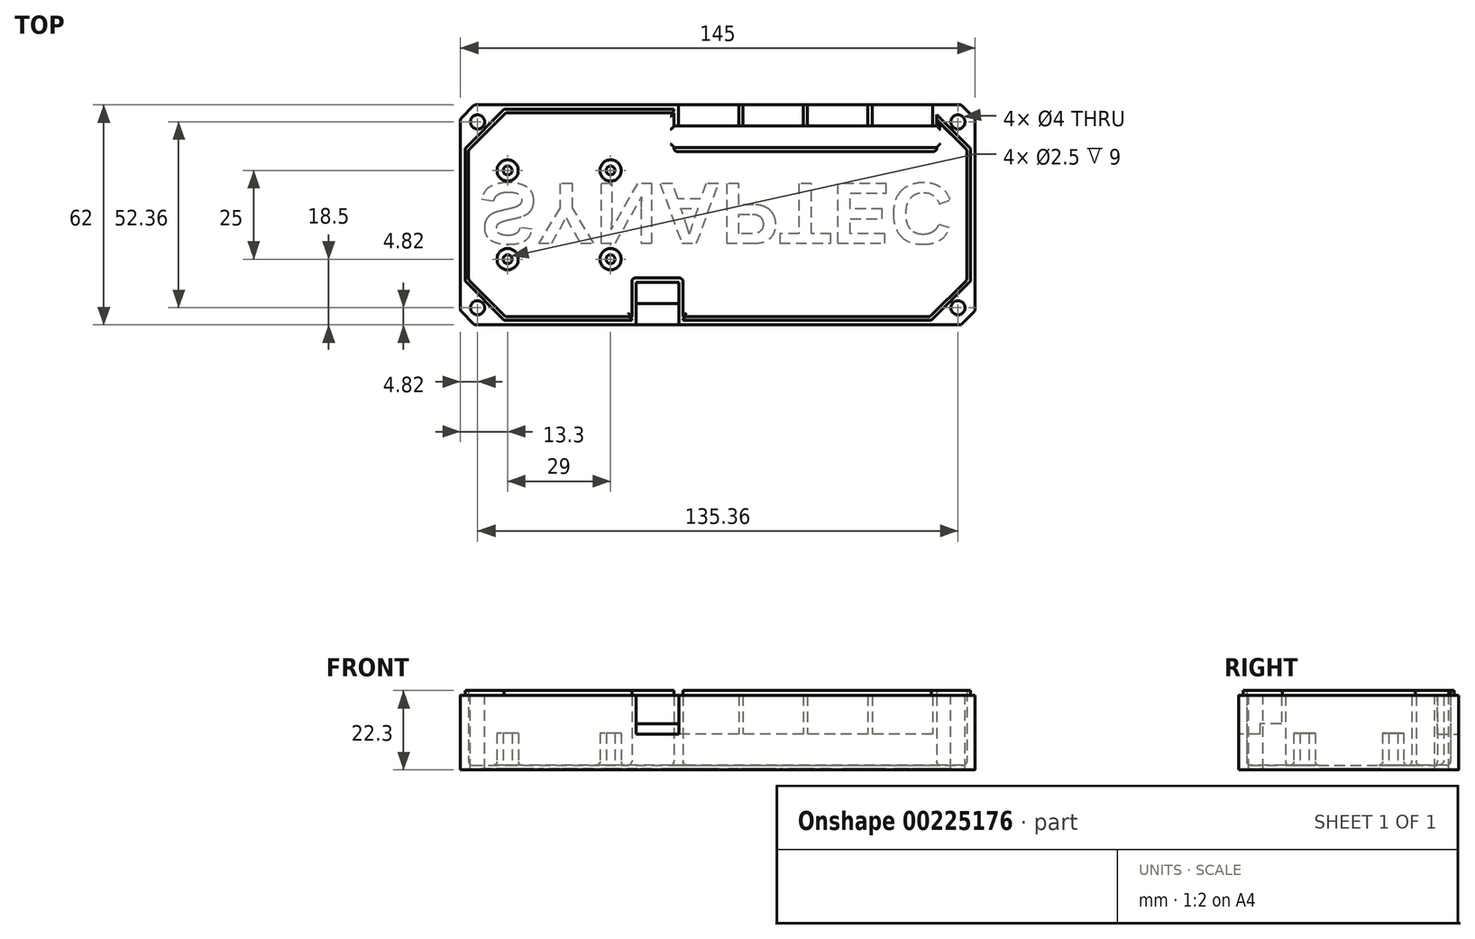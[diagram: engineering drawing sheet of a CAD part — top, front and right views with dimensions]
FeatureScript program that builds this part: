
annotation { "Feature Type Name" : "Feature", "Feature Type Description" : "" }
export const myFeature = defineFeature(function(context is Context, id is Id, definition is map)
    precondition{}
    {
        {
            var Q0;
            Q0=qCreatedBy(makeId("Top.planeOp"),FACE);
            var sketch = newSketch(context, id + "F0", { "sketchPlane" : qUnion([Q0])});
            skLineSegment(sketch, "E0.bottom", {"start": v(72.5, -31) * mm, "end": v(-72.5, -31) * mm});
            skLineSegment(sketch, "E0.top", {"start": v(72.5, 31) * mm, "end": v(-72.5, 31) * mm});
            skLineSegment(sketch, "E0.left", {"start": v(72.5, -31) * mm, "end": v(72.5, 31) * mm});
            skLineSegment(sketch, "E0.right", {"start": v(-72.5, -31) * mm, "end": v(-72.5, 31) * mm});
            skPoint(sketch, "E0.middle", {"position": v(0, 0) * mm});
            skSolve(sketch);
        }
        {
            var Q0;
            Q0=qSketchRegion(id+"F0",true);
            extrude(context, id + "F1", {"entities" : qUnion([Q0]), "depth" : 21 * mm});
        }
        {
            var Q0;
            Q0=makeQuery(id+"F1.opExtrude","CAP_FACE",FACE,{"disambiguationData":[OSD([sQuery(id+"F0.wireOp",EDGE,"E0.bottom"),sQuery(id+"F0.wireOp",EDGE,"E0.top"),sQuery(id+"F0.wireOp",EDGE,"E0.left"),sQuery(id+"F0.wireOp",EDGE,"E0.right")])],"isStart":false});
            var Q1;
            Q1=makeQuery(id+"F1.opExtrude","SWEPT_BODY",BODY,{"disambiguationData":[OSD([sQuery(id+"F0.wireOp",EDGE,"E0.bottom"),sQuery(id+"F0.wireOp",EDGE,"E0.top"),sQuery(id+"F0.wireOp",EDGE,"E0.left"),sQuery(id+"F0.wireOp",EDGE,"E0.right")])]});
            shell(context, id + "F2", {"entities" : qUnion([Q0]), "parts" : qUnion([Q1]), "thickness" : 1.3 * mm});
        }
        {
            var Q0;
            Q0=makeQuery(id+"F2.opShell","OFFSET_EDGE",EDGE,{"disambiguationData":[OSD([sQuery(id+"F0.wireOp",EDGE,"E0.top"),sQuery(id+"F0.wireOp",EDGE,"E0.left")])]});
            var Q1;
            Q1=makeQuery(id+"F2.opShell","OFFSET_EDGE",EDGE,{"disambiguationData":[OSD([sQuery(id+"F0.wireOp",EDGE,"E0.top"),sQuery(id+"F0.wireOp",EDGE,"E0.right")])]});
            var Q2;
            Q2=makeQuery(id+"F2.opShell","OFFSET_EDGE",EDGE,{"disambiguationData":[OSD([sQuery(id+"F0.wireOp",EDGE,"E0.bottom"),sQuery(id+"F0.wireOp",EDGE,"E0.right")])]});
            var Q3;
            Q3=makeQuery(id+"F2.opShell","OFFSET_EDGE",EDGE,{"disambiguationData":[OSD([sQuery(id+"F0.wireOp",EDGE,"E0.bottom"),sQuery(id+"F0.wireOp",EDGE,"E0.left")])]});
            chamfer(context, id + "F3", {"entities" : qUnion([Q0, Q1, Q2, Q3]), "width" : 11 * mm, "tangentPropagation" : true});
        }
        {
            var Q0;
            Q0=makeQuery(id+"F1.opExtrude","SWEPT_EDGE",EDGE,{"disambiguationData":[OSD([sQuery(id+"F0.wireOp",EDGE,"E0.top"),sQuery(id+"F0.wireOp",EDGE,"E0.right")])]});
            var Q1;
            Q1=makeQuery(id+"F1.opExtrude","SWEPT_EDGE",EDGE,{"disambiguationData":[OSD([sQuery(id+"F0.wireOp",EDGE,"E0.bottom"),sQuery(id+"F0.wireOp",EDGE,"E0.right")])]});
            var Q2;
            Q2=makeQuery(id+"F1.opExtrude","SWEPT_EDGE",EDGE,{"disambiguationData":[OSD([sQuery(id+"F0.wireOp",EDGE,"E0.top"),sQuery(id+"F0.wireOp",EDGE,"E0.left")])]});
            var Q3;
            Q3=makeQuery(id+"F1.opExtrude","SWEPT_EDGE",EDGE,{"disambiguationData":[OSD([sQuery(id+"F0.wireOp",EDGE,"E0.bottom"),sQuery(id+"F0.wireOp",EDGE,"E0.left")])]});
            chamfer(context, id + "F4", {"entities" : qUnion([Q0, Q1, Q2, Q3]), "width" : 4 * mm, "tangentPropagation" : true});
        }
        {
            var Q0;
            Q0=makeQuery(id+"F1.opExtrude","CAP_FACE",FACE,{"disambiguationData":[OSD([sQuery(id+"F0.wireOp",EDGE,"E0.bottom"),sQuery(id+"F0.wireOp",EDGE,"E0.top"),sQuery(id+"F0.wireOp",EDGE,"E0.left"),sQuery(id+"F0.wireOp",EDGE,"E0.right")])],"isStart":false});
            var sketch = newSketch(context, id + "F5", { "sketchPlane" : qUnion([Q0])});
            skCircle(sketch, "E1", {"center": v(-67.68, -26.18) * mm, "radius": 2 * mm});
            skCircle(sketch, "E2", {"center": v(-67.68, 26.18) * mm, "radius": 2 * mm});
            skCircle(sketch, "E3", {"center": v(67.68, 26.18) * mm, "radius": 2 * mm});
            skCircle(sketch, "E4", {"center": v(67.68, -26.18) * mm, "radius": 2 * mm});
            skLineSegment(sketch, "E5", {"start": v(-70.5, -29) * mm, "end": v(-65.7, -24.2) * mm, "construction": true});
            skLineSegment(sketch, "E6", {"start": v(-70.5, 29) * mm, "end": v(-65.7, 24.2) * mm, "construction": true});
            skLineSegment(sketch, "E7", {"start": v(70.5, 29) * mm, "end": v(65.7, 24.2) * mm, "construction": true});
            skLineSegment(sketch, "E8", {"start": v(70.5, -29) * mm, "end": v(65.7, -24.2) * mm, "construction": true});
            skSolve(sketch);
        }
        {
            var Q0;
            Q0=makeQuery(id+"F5.imprint","IMPRINT",FACE,{"disambiguationData":[TD([[makeQuery(id+"F5.imprint","IMPRINT",EDGE,{"derivedFrom":sQuery(id+"F5.wireOp",EDGE,"E2")}),1.0]])]});
            var Q1;
            Q1=makeQuery(id+"F5.imprint","IMPRINT",FACE,{"disambiguationData":[TD([[makeQuery(id+"F5.imprint","IMPRINT",EDGE,{"derivedFrom":sQuery(id+"F5.wireOp",EDGE,"E1")}),1.0]])]});
            var Q2;
            Q2=makeQuery(id+"F5.imprint","IMPRINT",FACE,{"disambiguationData":[TD([[makeQuery(id+"F5.imprint","IMPRINT",EDGE,{"derivedFrom":sQuery(id+"F5.wireOp",EDGE,"E4")}),1.0]])]});
            var Q3;
            Q3=makeQuery(id+"F5.imprint","IMPRINT",FACE,{"disambiguationData":[TD([[makeQuery(id+"F5.imprint","IMPRINT",EDGE,{"derivedFrom":sQuery(id+"F5.wireOp",EDGE,"E3")}),1.0]])]});
            extrude(context, id + "F6", {"entities" : qUnion([Q0, Q1, Q2, Q3]), "operationType" : NewBodyOperationType.REMOVE, "endBound" : BoundingType.UP_TO_NEXT, "oppositeDirection" : true, "depth" : 15 * mm});
        }
        {
            var Q0;
            Q0=makeQuery(id+"F2.opShell","OFFSET_FACE",FACE,{"disambiguationData":[OSD([sQuery(id+"F0.wireOp",EDGE,"E0.bottom"),sQuery(id+"F0.wireOp",EDGE,"E0.top"),sQuery(id+"F0.wireOp",EDGE,"E0.left"),sQuery(id+"F0.wireOp",EDGE,"E0.right")])]});
            var sketch = newSketch(context, id + "F7", { "sketchPlane" : qUnion([Q0])});
            skCircle(sketch, "E9", {"center": v(-30.2, -12.5) * mm, "radius": 3 * mm});
            skCircle(sketch, "E10.0", {"center": v(-30.2, -12.5) * mm, "radius": 1.25 * mm});
            skCircle(sketch, "E11.0.1.0", {"center": v(-30.2, 12.5) * mm, "radius": 3 * mm});
            skCircle(sketch, "E11.0.1.1", {"center": v(-30.2, 12.5) * mm, "radius": 1.25 * mm});
            skCircle(sketch, "E11.1.0.0", {"center": v(-59.2, -12.5) * mm, "radius": 3 * mm});
            skCircle(sketch, "E11.1.0.1", {"center": v(-59.2, -12.5) * mm, "radius": 1.25 * mm});
            skCircle(sketch, "E11.1.1.0", {"center": v(-59.2, 12.5) * mm, "radius": 3 * mm});
            skCircle(sketch, "E11.1.1.1", {"center": v(-59.2, 12.5) * mm, "radius": 1.25 * mm});
            skLineSegment(sketch, "E11.direction1", {"start": v(-30.2, -12.5) * mm, "end": v(-59.2, -12.5) * mm, "construction": true});
            skLineSegment(sketch, "E11.direction2", {"start": v(-30.2, -12.5) * mm, "end": v(-30.2, 12.5) * mm, "construction": true});
            skLineSegment(sketch, "E12.right", {"start": v(71.2, 18) * mm, "end": v(71.2, 16.8) * mm});
            skLineSegment(sketch, "E13.bottom", {"start": v(61.7, 29.7) * mm, "end": v(-12.3, 29.7) * mm});
            skLineSegment(sketch, "E13.top", {"start": v(61.7, 25) * mm, "end": v(-12.3, 25) * mm});
            skLineSegment(sketch, "E13.left", {"start": v(61.7, 29.7) * mm, "end": v(61.7, 25) * mm});
            skLineSegment(sketch, "E13.right", {"start": v(-12.3, 29.7) * mm, "end": v(-12.3, 25) * mm});
            skLineSegment(sketch, "E14.bottom", {"start": v(-12.3, 25) * mm, "end": v(61.7, 25) * mm});
            skLineSegment(sketch, "E14.top", {"start": v(-12.3, 19) * mm, "end": v(61.7, 19) * mm});
            skLineSegment(sketch, "E14.left", {"start": v(-12.3, 25) * mm, "end": v(-12.3, 19) * mm});
            skLineSegment(sketch, "E14.right", {"start": v(61.7, 25) * mm, "end": v(61.7, 19) * mm});
            skLineSegment(sketch, "E15.top", {"start": v(-12.3, 17.8) * mm, "end": v(61.7, 17.8) * mm});
            skLineSegment(sketch, "E15.left", {"start": v(-12.3, 19) * mm, "end": v(-12.3, 17.8) * mm});
            skLineSegment(sketch, "E15.right", {"start": v(61.7, 19) * mm, "end": v(61.7, 17.8) * mm});
            skLineSegment(sketch, "E16.bottom", {"start": v(-24.2, -29.7) * mm, "end": v(-9.8, -29.7) * mm});
            skLineSegment(sketch, "E16.top", {"start": v(-24.2, -25) * mm, "end": v(-9.8, -25) * mm});
            skLineSegment(sketch, "E16.left", {"start": v(-24.2, -29.7) * mm, "end": v(-24.2, -25) * mm});
            skLineSegment(sketch, "E16.right", {"start": v(-9.8, -29.7) * mm, "end": v(-9.8, -25) * mm});
            skLineSegment(sketch, "E17.top", {"start": v(-24.2, -19) * mm, "end": v(-9.8, -19) * mm});
            skLineSegment(sketch, "E17.left", {"start": v(-24.2, -25) * mm, "end": v(-24.2, -19) * mm});
            skLineSegment(sketch, "E17.right", {"start": v(-9.8, -25) * mm, "end": v(-9.8, -19) * mm});
            skLineSegment(sketch, "E18.top", {"start": v(-24.2, -17.8) * mm, "end": v(-9.8, -17.8) * mm});
            skLineSegment(sketch, "E18.left", {"start": v(-24.2, -19) * mm, "end": v(-24.2, -17.8) * mm});
            skLineSegment(sketch, "E18.right", {"start": v(-9.8, -19) * mm, "end": v(-9.8, -17.8) * mm});
            skSolve(sketch);
        }
        {
            var Q0;
            Q0=makeQuery(id+"F7.imprint","IMPRINT",FACE,{"disambiguationData":[TD([[makeQuery(id+"F7.imprint","IMPRINT",EDGE,{"derivedFrom":sQuery(id+"F7.wireOp",EDGE,"E9")}),1.0]])]});
            var Q1;
            Q1=makeQuery(id+"F7.imprint","IMPRINT",FACE,{"disambiguationData":[TD([[makeQuery(id+"F7.imprint","IMPRINT",EDGE,{"derivedFrom":sQuery(id+"F7.wireOp",EDGE,"E11.0.1.0")}),1.0]])]});
            var Q2;
            Q2=makeQuery(id+"F7.imprint","IMPRINT",FACE,{"disambiguationData":[TD([[makeQuery(id+"F7.imprint","IMPRINT",EDGE,{"derivedFrom":sQuery(id+"F7.wireOp",EDGE,"E11.1.1.0")}),1.0]])]});
            var Q3;
            Q3=makeQuery(id+"F7.imprint","IMPRINT",FACE,{"disambiguationData":[TD([[makeQuery(id+"F7.imprint","IMPRINT",EDGE,{"derivedFrom":sQuery(id+"F7.wireOp",EDGE,"E11.1.0.0")}),1.0]])]});
            var Q4;
            Q4=makeQuery(id+"F7.imprint","IMPRINT",FACE,{"disambiguationData":[TD([[makeQuery(id+"F7.imprint","IMPRINT",EDGE,{"derivedFrom":sQuery(id+"F7.wireOp",EDGE,"42ae70fa-aec6-44d3-95c4-a3b67ad8d79e.1.1.0")}),1.0]])]});
            var Q5;
            Q5=makeQuery(id+"F7.imprint","IMPRINT",FACE,{"disambiguationData":[TD([[makeQuery(id+"F7.imprint","IMPRINT",EDGE,{"derivedFrom":sQuery(id+"F7.wireOp",EDGE,"42ae70fa-aec6-44d3-95c4-a3b67ad8d79e.0.1.0")}),1.0]])]});
            var Q6;
            Q6=makeQuery(id+"F7.imprint","IMPRINT",FACE,{"disambiguationData":[TD([[makeQuery(id+"F7.imprint","IMPRINT",EDGE,{"derivedFrom":sQuery(id+"F7.wireOp",EDGE,"ABs4xrQX-9s09-FMAu-MQul-4i9KuJrflMF1.bottom")}),-1.0]])]});
            var Q7;
            Q7=makeQuery(id+"F7.imprint","IMPRINT",FACE,{"disambiguationData":[TD([[makeQuery(id+"F7.imprint","IMPRINT",EDGE,{"derivedFrom":sQuery(id+"F7.wireOp",EDGE,"42ae70fa-aec6-44d3-95c4-a3b67ad8d79e.1.0.0")}),1.0]])]});
            extrude(context, id + "F8", {"entities" : qUnion([Q0, Q1, Q2, Q3, Q4, Q5, Q6, Q7]), "operationType" : NewBodyOperationType.ADD, "depth" : 9 * mm});
        }
        {
            var Q0;
            Q0=makeQuery(id+"F7.imprint","IMPRINT",FACE,{"disambiguationData":[TD([[makeQuery(id+"F7.imprint","IMPRINT",EDGE,{"derivedFrom":sQuery(id+"F7.wireOp",EDGE,"E13.bottom")}),1.0]])]});
            var Q1;
            Q1=makeQuery(id+"F7.imprint","IMPRINT",FACE,{"disambiguationData":[TD([[makeQuery(id+"F7.imprint","IMPRINT",EDGE,{"derivedFrom":sQuery(id+"F7.wireOp",EDGE,"E14.bottom")}),-1.0]])]});
            var Q2;
            Q2=makeQuery(id+"F7.imprint","IMPRINT",FACE,{"disambiguationData":[TD([[makeQuery(id+"F7.imprint","IMPRINT",EDGE,{"derivedFrom":sQuery(id+"F7.wireOp",EDGE,"E14.top")}),-1.0]])]});
            var Q3;
            Q3=makeQuery(id+"F7.imprint","IMPRINT",FACE,{"disambiguationData":[TD([[makeQuery(id+"F7.imprint","IMPRINT",EDGE,{"derivedFrom":sQuery(id+"F7.wireOp",EDGE,"E16.bottom")}),-1.0]])]});
            var Q4;
            Q4=makeQuery(id+"F7.imprint","IMPRINT",FACE,{"disambiguationData":[TD([[makeQuery(id+"F7.imprint","IMPRINT",EDGE,{"derivedFrom":sQuery(id+"F7.wireOp",EDGE,"E16.top")}),1.0]])]});
            var Q5;
            Q5=makeQuery(id+"F7.imprint","IMPRINT",FACE,{"disambiguationData":[TD([[makeQuery(id+"F7.imprint","IMPRINT",EDGE,{"derivedFrom":sQuery(id+"F7.wireOp",EDGE,"E17.top")}),1.0]])]});
            var Q6;
            {var subQ1=sQuery(id+"F7.wireOp",EDGE,"E13.right");Q6=makeQuery(id+"F7.imprint","IMPRINT",FACE,{"disambiguationData":[TD([[makeQuery(id+"F7.imprint","IMPRINT",EDGE,{"derivedFrom":subQ1}),1.0]])]});}
            var Q7;
            Q7=makeQuery(id+"F1.opExtrude","CAP_FACE",FACE,{"disambiguationData":[OSD([sQuery(id+"F0.wireOp",EDGE,"E0.bottom"),sQuery(id+"F0.wireOp",EDGE,"E0.top"),sQuery(id+"F0.wireOp",EDGE,"E0.left"),sQuery(id+"F0.wireOp",EDGE,"E0.right")])],"isStart":false});
            extrude(context, id + "F9", {"entities" : qUnion([Q0, Q1, Q2, Q3, Q4, Q5, Q6]), "operationType" : NewBodyOperationType.ADD, "endBound" : BoundingType.UP_TO_SURFACE, "endBoundEntityFace" : qUnion([Q7]), "depth" : 15 * mm});
        }
        {
            var Q0;
            {var subQ0=sQuery(id+"F0.wireOp",EDGE,"E0.right");var subQ1=sQuery(id+"F0.wireOp",EDGE,"E0.top");var subQ2=sQuery(id+"F0.wireOp",EDGE,"E0.left");var subQ3=sQuery(id+"F0.wireOp",EDGE,"E0.bottom");Q0=makeQuery(id+"F8.boolean.opBoolean","SPLIT",FACE,{"disambiguationData":[TD([makeQuery(id+"F2.opShell","OFFSET_FACE",FACE,{"disambiguationData":[OSD([subQ3])]})])],"derivedFrom":makeQuery(id+"F2.opShell","OFFSET_FACE",FACE,{"disambiguationData":[OSD([subQ3,subQ1,subQ2,subQ0])]})});}
            var sketch = newSketch(context, id + "F10", { "sketchPlane" : qUnion([Q0])});
            skLineSegment(sketch, "E19.2", {"start": v(-59.79, -28.7) * mm, "end": v(-24.2, -28.7) * mm});
            skLineSegment(sketch, "E19.3", {"start": v(-70.2, -18.29) * mm, "end": v(-59.79, -28.7) * mm});
            skLineSegment(sketch, "E19.4", {"start": v(70.2, 18.29) * mm, "end": v(61.7, 26.79) * mm});
            skLineSegment(sketch, "E19.5", {"start": v(70.2, -18.29) * mm, "end": v(70.2, 18.29) * mm});
            skLineSegment(sketch, "E19.6", {"start": v(59.79, -28.7) * mm, "end": v(70.2, -18.29) * mm});
            skLineSegment(sketch, "E19.7", {"start": v(-9.8, -28.7) * mm, "end": v(59.79, -28.7) * mm});
            skLineSegment(sketch, "E19.11", {"start": v(-12.3, 28.7) * mm, "end": v(-59.79, 28.7) * mm});
            skLineSegment(sketch, "E19.13", {"start": v(-59.79, 28.7) * mm, "end": v(-70.2, 18.29) * mm});
            skLineSegment(sketch, "E19.14", {"start": v(-70.2, 18.29) * mm, "end": v(-70.2, -18.29) * mm});
            skSolve(sketch);
        }
        {
            var Q0;
            Q0=makeQuery(id+"F10.imprint","IMPRINT",FACE,{"disambiguationData":[TD([[makeQuery(id+"F10.imprint","IMPRINT",EDGE,{"derivedFrom":sQuery(id+"F10.wireOp",EDGE,"E19.0")}),-1.0]])]});
            var Q1;
            {var subQ9=sQuery(id+"F10.wireOp",EDGE,"E19.2");Q1=makeQuery(id+"F10.imprint","IMPRINT",FACE,{"disambiguationData":[TD([[makeQuery(id+"F10.imprint","IMPRINT",EDGE,{"derivedFrom":subQ9}),-1.0]])]});}
            var Q2;
            {var subQ9=sQuery(id+"F10.wireOp",EDGE,"E19.4");Q2=makeQuery(id+"F10.imprint","IMPRINT",FACE,{"disambiguationData":[TD([[makeQuery(id+"F10.imprint","IMPRINT",EDGE,{"derivedFrom":subQ9}),-1.0]])]});}
            extrude(context, id + "F11", {"entities" : qUnion([Q0, Q1, Q2]), "operationType" : NewBodyOperationType.ADD, "depth" : 21 * mm});
        }
        {
            var Q0;
            Q0=makeQuery(id+"F1.opExtrude","SWEPT_FACE",FACE,{"disambiguationData":[OSD([sQuery(id+"F0.wireOp",EDGE,"E0.top")])]});
            var sketch = newSketch(context, id + "F12", { "sketchPlane" : qUnion([Q0])});
            skLineSegment(sketch, "E20.bottom", {"start": v(-60.5, 21) * mm, "end": v(-43.5, 21) * mm});
            skLineSegment(sketch, "E20.top", {"start": v(-60.5, 10) * mm, "end": v(-43.5, 10) * mm});
            skLineSegment(sketch, "E20.left", {"start": v(-60.5, 21) * mm, "end": v(-60.5, 10) * mm});
            skLineSegment(sketch, "E20.right", {"start": v(-43.5, 21) * mm, "end": v(-43.5, 10) * mm});
            skLineSegment(sketch, "E21", {"start": v(-60.5, 13) * mm, "end": v(-43.5, 13) * mm});
            skLineSegment(sketch, "E22.1.0.0", {"start": v(-42.3, 21) * mm, "end": v(-42.3, 10) * mm});
            skLineSegment(sketch, "E22.1.0.1", {"start": v(-25.3, 21) * mm, "end": v(-25.3, 10) * mm});
            skLineSegment(sketch, "E22.1.0.2", {"start": v(-42.3, 13) * mm, "end": v(-25.3, 13) * mm});
            skLineSegment(sketch, "E22.1.0.3", {"start": v(-42.3, 10) * mm, "end": v(-25.3, 10) * mm});
            skLineSegment(sketch, "E22.1.0.4", {"start": v(-42.3, 21) * mm, "end": v(-25.3, 21) * mm});
            skLineSegment(sketch, "E22.2.0.0", {"start": v(-24.1, 21) * mm, "end": v(-24.1, 10) * mm});
            skLineSegment(sketch, "E22.2.0.1", {"start": v(-7.1, 21) * mm, "end": v(-7.1, 10) * mm});
            skLineSegment(sketch, "E22.2.0.2", {"start": v(-24.1, 13) * mm, "end": v(-7.1, 13) * mm});
            skLineSegment(sketch, "E22.2.0.3", {"start": v(-24.1, 10) * mm, "end": v(-7.1, 10) * mm});
            skLineSegment(sketch, "E22.2.0.4", {"start": v(-24.1, 21) * mm, "end": v(-7.1, 21) * mm});
            skLineSegment(sketch, "E22.3.0.0", {"start": v(-5.9, 21) * mm, "end": v(-5.9, 10) * mm});
            skLineSegment(sketch, "E22.3.0.1", {"start": v(11.1, 21) * mm, "end": v(11.1, 10) * mm});
            skLineSegment(sketch, "E22.3.0.2", {"start": v(-5.9, 13) * mm, "end": v(11.1, 13) * mm});
            skLineSegment(sketch, "E22.3.0.3", {"start": v(-5.9, 10) * mm, "end": v(11.1, 10) * mm});
            skLineSegment(sketch, "E22.3.0.4", {"start": v(-5.9, 21) * mm, "end": v(11.1, 21) * mm});
            skLineSegment(sketch, "E22.direction1", {"start": v(-60.5, 10) * mm, "end": v(-42.3, 10) * mm, "construction": true});
            skSolve(sketch);
        }
        {
            var Q0;
            {var subQ0=sQuery(id+"F12.wireOp",EDGE,"E21");Q0=makeQuery(id+"F12.imprint","IMPRINT",FACE,{"disambiguationData":[TD([[makeQuery(id+"F12.imprint","IMPRINT",EDGE,{"derivedFrom":subQ0}),1.0]])]});}
            var Q1;
            {var subQ0=sQuery(id+"F12.wireOp",EDGE,"E22.1.0.2");Q1=makeQuery(id+"F12.imprint","IMPRINT",FACE,{"disambiguationData":[TD([[makeQuery(id+"F12.imprint","IMPRINT",EDGE,{"derivedFrom":subQ0}),1.0]])]});}
            var Q2;
            {var subQ0=sQuery(id+"F12.wireOp",EDGE,"E22.2.0.2");Q2=makeQuery(id+"F12.imprint","IMPRINT",FACE,{"disambiguationData":[TD([[makeQuery(id+"F12.imprint","IMPRINT",EDGE,{"derivedFrom":subQ0}),1.0]])]});}
            var Q3;
            {var subQ0=sQuery(id+"F12.wireOp",EDGE,"E22.3.0.2");Q3=makeQuery(id+"F12.imprint","IMPRINT",FACE,{"disambiguationData":[TD([[makeQuery(id+"F12.imprint","IMPRINT",EDGE,{"derivedFrom":subQ0}),1.0]])]});}
            var Q4;
            {var subQ0=sQuery(id+"F12.wireOp",EDGE,"E22.3.0.4");Q4=makeQuery(id+"F12.imprint","IMPRINT",FACE,{"disambiguationData":[TD([[makeQuery(id+"F12.imprint","IMPRINT",EDGE,{"derivedFrom":subQ0}),-1.0]])]});}
            var Q5;
            {var subQ0=sQuery(id+"F12.wireOp",EDGE,"E22.2.0.4");Q5=makeQuery(id+"F12.imprint","IMPRINT",FACE,{"disambiguationData":[TD([[makeQuery(id+"F12.imprint","IMPRINT",EDGE,{"derivedFrom":subQ0}),-1.0]])]});}
            var Q6;
            {var subQ0=sQuery(id+"F12.wireOp",EDGE,"E22.1.0.4");Q6=makeQuery(id+"F12.imprint","IMPRINT",FACE,{"disambiguationData":[TD([[makeQuery(id+"F12.imprint","IMPRINT",EDGE,{"derivedFrom":subQ0}),-1.0]])]});}
            var Q7;
            {var subQ0=sQuery(id+"F12.wireOp",EDGE,"E20.bottom");Q7=makeQuery(id+"F12.imprint","IMPRINT",FACE,{"disambiguationData":[TD([[makeQuery(id+"F12.imprint","IMPRINT",EDGE,{"derivedFrom":subQ0}),-1.0]])]});}
            extrude(context, id + "F13", {"entities" : qUnion([Q0, Q1, Q2, Q3, Q4, Q5, Q6, Q7]), "operationType" : NewBodyOperationType.REMOVE, "oppositeDirection" : true, "depth" : 12 * mm});
        }
        {
            var Q0;
            {var subQ0=sQuery(id+"F12.wireOp",EDGE,"E20.top");Q0=makeQuery(id+"F12.imprint","IMPRINT",FACE,{"disambiguationData":[TD([[makeQuery(id+"F12.imprint","IMPRINT",EDGE,{"derivedFrom":subQ0}),1.0]])]});}
            var Q1;
            {var subQ2=sQuery(id+"F12.wireOp",EDGE,"E22.1.0.2");Q1=makeQuery(id+"F12.imprint","IMPRINT",FACE,{"disambiguationData":[TD([[makeQuery(id+"F12.imprint","IMPRINT",EDGE,{"derivedFrom":subQ2}),-1.0]])]});}
            var Q2;
            {var subQ2=sQuery(id+"F12.wireOp",EDGE,"E22.2.0.2");Q2=makeQuery(id+"F12.imprint","IMPRINT",FACE,{"disambiguationData":[TD([[makeQuery(id+"F12.imprint","IMPRINT",EDGE,{"derivedFrom":subQ2}),-1.0]])]});}
            var Q3;
            {var subQ2=sQuery(id+"F12.wireOp",EDGE,"E22.3.0.2");Q3=makeQuery(id+"F12.imprint","IMPRINT",FACE,{"disambiguationData":[TD([[makeQuery(id+"F12.imprint","IMPRINT",EDGE,{"derivedFrom":subQ2}),-1.0]])]});}
            extrude(context, id + "F14", {"entities" : qUnion([Q0, Q1, Q2, Q3]), "operationType" : NewBodyOperationType.REMOVE, "oppositeDirection" : true, "depth" : 6 * mm});
        }
        {
            var Q0;
            Q0=makeQuery(id+"F1.opExtrude","SWEPT_FACE",FACE,{"disambiguationData":[OSD([sQuery(id+"F0.wireOp",EDGE,"E0.bottom")])]});
            var sketch = newSketch(context, id + "F15", { "sketchPlane" : qUnion([Q0])});
            skLineSegment(sketch, "E23.bottom", {"start": v(-23, 21) * mm, "end": v(-11, 21) * mm});
            skLineSegment(sketch, "E23.top", {"start": v(-23, 10) * mm, "end": v(-11, 10) * mm});
            skLineSegment(sketch, "E23.left", {"start": v(-23, 21) * mm, "end": v(-23, 10) * mm});
            skLineSegment(sketch, "E23.right", {"start": v(-11, 21) * mm, "end": v(-11, 10) * mm});
            skLineSegment(sketch, "E24", {"start": v(-23, 13) * mm, "end": v(-11, 13) * mm});
            skSolve(sketch);
        }
        {
            var Q0;
            {var subQ0=sQuery(id+"F15.wireOp",EDGE,"E23.top");Q0=makeQuery(id+"F15.imprint","IMPRINT",FACE,{"disambiguationData":[TD([[makeQuery(id+"F15.imprint","IMPRINT",EDGE,{"derivedFrom":subQ0}),1.0]])]});}
            extrude(context, id + "F16", {"entities" : qUnion([Q0]), "operationType" : NewBodyOperationType.REMOVE, "oppositeDirection" : true, "depth" : 6 * mm});
        }
        {
            var Q0;
            {var subQ0=sQuery(id+"F15.wireOp",EDGE,"E23.bottom");Q0=makeQuery(id+"F15.imprint","IMPRINT",FACE,{"disambiguationData":[TD([[makeQuery(id+"F15.imprint","IMPRINT",EDGE,{"derivedFrom":subQ0}),1.0]])]});}
            extrude(context, id + "F17", {"entities" : qUnion([Q0]), "operationType" : NewBodyOperationType.REMOVE, "oppositeDirection" : true, "depth" : 12 * mm});
        }
        {
            var Q0;
            {var subQ0=sQuery(id+"F0.wireOp",EDGE,"E0.right");var subQ1=sQuery(id+"F0.wireOp",EDGE,"E0.top");var subQ2=sQuery(id+"F0.wireOp",EDGE,"E0.left");var subQ3=sQuery(id+"F0.wireOp",EDGE,"E0.bottom");Q0=makeQuery(id+"F8.boolean.opBoolean","SPLIT",FACE,{"disambiguationData":[TD([makeQuery(id+"F2.opShell","OFFSET_FACE",FACE,{"disambiguationData":[OSD([subQ3])]})])],"derivedFrom":makeQuery(id+"F2.opShell","OFFSET_FACE",FACE,{"disambiguationData":[OSD([subQ3,subQ1,subQ2,subQ0])]})});}
            var Q1;
            {var subQ0=sQuery(id+"F0.wireOp",EDGE,"E0.right");Q1=makeQuery(id+"F4.opChamfer","BLEND_EDGE",EDGE,{"blendedFrom":[makeQuery(id+"F1.opExtrude","SWEPT_EDGE",EDGE,{"disambiguationData":[OSD([sQuery(id+"F0.wireOp",EDGE,"E0.bottom"),subQ0])]}),makeQuery(id+"F1.opExtrude","SWEPT_FACE",FACE,{"disambiguationData":[OSD([subQ0])]})],"blendedInto":[makeQuery(id+"F1.opExtrude","SWEPT_FACE",FACE,{"disambiguationData":[OSD([subQ0])]})]});}
            var Q2;
            {var subQ0=sQuery(id+"F0.wireOp",EDGE,"E0.bottom");Q2=makeQuery(id+"F4.opChamfer","BLEND_EDGE",EDGE,{"blendedFrom":[makeQuery(id+"F1.opExtrude","SWEPT_EDGE",EDGE,{"disambiguationData":[OSD([subQ0,sQuery(id+"F0.wireOp",EDGE,"E0.right")])]}),makeQuery(id+"F1.opExtrude","SWEPT_FACE",FACE,{"disambiguationData":[OSD([subQ0])]})],"blendedInto":[makeQuery(id+"F1.opExtrude","SWEPT_FACE",FACE,{"disambiguationData":[OSD([subQ0])]})]});}
            var Q3;
            {var subQ0=sQuery(id+"F0.wireOp",EDGE,"E0.bottom");Q3=makeQuery(id+"F4.opChamfer","BLEND_EDGE",EDGE,{"blendedFrom":[makeQuery(id+"F1.opExtrude","SWEPT_EDGE",EDGE,{"disambiguationData":[OSD([subQ0,sQuery(id+"F0.wireOp",EDGE,"E0.left")])]}),makeQuery(id+"F1.opExtrude","SWEPT_FACE",FACE,{"disambiguationData":[OSD([subQ0])]})],"blendedInto":[makeQuery(id+"F1.opExtrude","SWEPT_FACE",FACE,{"disambiguationData":[OSD([subQ0])]})]});}
            var Q4;
            {var subQ0=sQuery(id+"F0.wireOp",EDGE,"E0.left");Q4=makeQuery(id+"F4.opChamfer","BLEND_EDGE",EDGE,{"blendedFrom":[makeQuery(id+"F1.opExtrude","SWEPT_EDGE",EDGE,{"disambiguationData":[OSD([sQuery(id+"F0.wireOp",EDGE,"E0.bottom"),subQ0])]}),makeQuery(id+"F1.opExtrude","SWEPT_FACE",FACE,{"disambiguationData":[OSD([subQ0])]})],"blendedInto":[makeQuery(id+"F1.opExtrude","SWEPT_FACE",FACE,{"disambiguationData":[OSD([subQ0])]})]});}
            var Q5;
            {var subQ0=sQuery(id+"F0.wireOp",EDGE,"E0.top");Q5=makeQuery(id+"F4.opChamfer","BLEND_EDGE",EDGE,{"blendedFrom":[makeQuery(id+"F1.opExtrude","SWEPT_EDGE",EDGE,{"disambiguationData":[OSD([subQ0,sQuery(id+"F0.wireOp",EDGE,"E0.right")])]}),makeQuery(id+"F1.opExtrude","SWEPT_FACE",FACE,{"disambiguationData":[OSD([subQ0])]})],"blendedInto":[makeQuery(id+"F1.opExtrude","SWEPT_FACE",FACE,{"disambiguationData":[OSD([subQ0])]})]});}
            var Q6;
            {var subQ0=sQuery(id+"F0.wireOp",EDGE,"E0.right");Q6=makeQuery(id+"F4.opChamfer","BLEND_EDGE",EDGE,{"blendedFrom":[makeQuery(id+"F1.opExtrude","SWEPT_EDGE",EDGE,{"disambiguationData":[OSD([sQuery(id+"F0.wireOp",EDGE,"E0.top"),subQ0])]}),makeQuery(id+"F1.opExtrude","SWEPT_FACE",FACE,{"disambiguationData":[OSD([subQ0])]})],"blendedInto":[makeQuery(id+"F1.opExtrude","SWEPT_FACE",FACE,{"disambiguationData":[OSD([subQ0])]})]});}
            var Q7;
            {var subQ0=sQuery(id+"F0.wireOp",EDGE,"E0.left");Q7=makeQuery(id+"F4.opChamfer","BLEND_EDGE",EDGE,{"blendedFrom":[makeQuery(id+"F1.opExtrude","SWEPT_EDGE",EDGE,{"disambiguationData":[OSD([sQuery(id+"F0.wireOp",EDGE,"E0.top"),subQ0])]}),makeQuery(id+"F1.opExtrude","SWEPT_FACE",FACE,{"disambiguationData":[OSD([subQ0])]})],"blendedInto":[makeQuery(id+"F1.opExtrude","SWEPT_FACE",FACE,{"disambiguationData":[OSD([subQ0])]})]});}
            var Q8;
            {var subQ0=sQuery(id+"F0.wireOp",EDGE,"E0.top");Q8=makeQuery(id+"F4.opChamfer","BLEND_EDGE",EDGE,{"blendedFrom":[makeQuery(id+"F1.opExtrude","SWEPT_EDGE",EDGE,{"disambiguationData":[OSD([subQ0,sQuery(id+"F0.wireOp",EDGE,"E0.left")])]}),makeQuery(id+"F1.opExtrude","SWEPT_FACE",FACE,{"disambiguationData":[OSD([subQ0])]})],"blendedInto":[makeQuery(id+"F1.opExtrude","SWEPT_FACE",FACE,{"disambiguationData":[OSD([subQ0])]})]});}
            var Q9;
            Q9=makeQuery(id+"F9.opExtrude","SWEPT_EDGE",EDGE,{"disambiguationData":[OSD([sQuery(id+"F7.wireOp",EDGE,"E18.top"),sQuery(id+"F7.wireOp",EDGE,"E18.right")])]});
            var Q10;
            Q10=makeQuery(id+"F9.opExtrude","SWEPT_EDGE",EDGE,{"disambiguationData":[OSD([sQuery(id+"F7.wireOp",EDGE,"E18.top"),sQuery(id+"F7.wireOp",EDGE,"E18.left")])]});
            var Q11;
            {var subQ0=sQuery(id+"F7.wireOp",EDGE,"E18.right");var subQ1=sQuery(id+"F7.wireOp",EDGE,"E17.right");var subQ2=sQuery(id+"F7.wireOp",EDGE,"E16.right");var subQ3=sQuery(id+"F0.wireOp",EDGE,"E0.right");var subQ4=sQuery(id+"F0.wireOp",EDGE,"E0.left");var subQ5=sQuery(id+"F0.wireOp",EDGE,"E0.top");var subQ6=sQuery(id+"F0.wireOp",EDGE,"E0.bottom");var subQ7=sQuery(id+"F10.wireOp",EDGE,"E19.7");Q11=makeQuery(id+"F11.boolean.opBoolean","SPLIT",EDGE,{"disambiguationData":[TD([makeQuery(id+"F2.opShell","OFFSET_FACE",FACE,{"disambiguationData":[OSD([subQ6,subQ5,subQ4,subQ3])]})])],"derivedFrom":makeQuery(id+"F11.opExtrude","SWEPT_EDGE",EDGE,{"disambiguationData":[OSD([subQ2,subQ1,subQ0,subQ7])]})});}
            var Q12;
            {var subQ0=sQuery(id+"F7.wireOp",EDGE,"E18.left");var subQ1=sQuery(id+"F7.wireOp",EDGE,"E17.left");var subQ2=sQuery(id+"F7.wireOp",EDGE,"E16.left");var subQ3=sQuery(id+"F0.wireOp",EDGE,"E0.right");var subQ4=sQuery(id+"F0.wireOp",EDGE,"E0.left");var subQ5=sQuery(id+"F0.wireOp",EDGE,"E0.top");var subQ6=sQuery(id+"F0.wireOp",EDGE,"E0.bottom");var subQ7=sQuery(id+"F10.wireOp",EDGE,"E19.2");Q12=makeQuery(id+"F11.boolean.opBoolean","SPLIT",EDGE,{"disambiguationData":[TD([makeQuery(id+"F2.opShell","OFFSET_FACE",FACE,{"disambiguationData":[OSD([subQ6,subQ5,subQ4,subQ3])]})])],"derivedFrom":makeQuery(id+"F11.opExtrude","SWEPT_EDGE",EDGE,{"disambiguationData":[OSD([subQ2,subQ1,subQ0,subQ7])]})});}
            var Q13;
            Q13=makeQuery(id+"F11.opExtrude","SWEPT_EDGE",EDGE,{"disambiguationData":[OSD([sQuery(id+"F10.wireOp",EDGE,"E19.2"),sQuery(id+"F10.wireOp",EDGE,"E19.3")])]});
            var Q14;
            Q14=makeQuery(id+"F11.opExtrude","SWEPT_EDGE",EDGE,{"disambiguationData":[OSD([sQuery(id+"F10.wireOp",EDGE,"E19.3"),sQuery(id+"F10.wireOp",EDGE,"E19.14")])]});
            var Q15;
            Q15=makeQuery(id+"F11.opExtrude","SWEPT_EDGE",EDGE,{"disambiguationData":[OSD([sQuery(id+"F10.wireOp",EDGE,"E19.13"),sQuery(id+"F10.wireOp",EDGE,"E19.14")])]});
            var Q16;
            Q16=makeQuery(id+"F11.opExtrude","SWEPT_EDGE",EDGE,{"disambiguationData":[OSD([sQuery(id+"F10.wireOp",EDGE,"E19.11"),sQuery(id+"F10.wireOp",EDGE,"E19.13")])]});
            var Q17;
            Q17=makeQuery(id+"F9.opExtrude","SWEPT_EDGE",EDGE,{"disambiguationData":[OSD([sQuery(id+"F7.wireOp",EDGE,"E15.top"),sQuery(id+"F7.wireOp",EDGE,"E15.left")])]});
            var Q18;
            Q18=makeQuery(id+"F9.opExtrude","SWEPT_EDGE",EDGE,{"disambiguationData":[OSD([sQuery(id+"F7.wireOp",EDGE,"E15.top"),sQuery(id+"F7.wireOp",EDGE,"E15.right")])]});
            var Q19;
            {var subQ0=sQuery(id+"F7.wireOp",EDGE,"E15.left");var subQ1=sQuery(id+"F7.wireOp",EDGE,"E14.left");var subQ2=sQuery(id+"F7.wireOp",EDGE,"E13.right");var subQ3=sQuery(id+"F0.wireOp",EDGE,"E0.right");var subQ4=sQuery(id+"F0.wireOp",EDGE,"E0.left");var subQ5=sQuery(id+"F0.wireOp",EDGE,"E0.top");var subQ6=sQuery(id+"F0.wireOp",EDGE,"E0.bottom");var subQ7=sQuery(id+"F10.wireOp",EDGE,"E19.11");Q19=makeQuery(id+"F11.boolean.opBoolean","SPLIT",EDGE,{"disambiguationData":[TD([makeQuery(id+"F2.opShell","OFFSET_FACE",FACE,{"disambiguationData":[OSD([subQ6,subQ5,subQ4,subQ3])]})])],"derivedFrom":makeQuery(id+"F11.opExtrude","SWEPT_EDGE",EDGE,{"disambiguationData":[OSD([subQ2,subQ1,subQ0,subQ7])]})});}
            var Q20;
            Q20=makeQuery(id+"F11.opExtrude","SWEPT_EDGE",EDGE,{"disambiguationData":[OSD([sQuery(id+"F10.wireOp",EDGE,"E19.4"),sQuery(id+"F10.wireOp",EDGE,"E19.5")])]});
            var Q21;
            Q21=makeQuery(id+"F11.opExtrude","SWEPT_EDGE",EDGE,{"disambiguationData":[OSD([sQuery(id+"F10.wireOp",EDGE,"E19.6"),sQuery(id+"F10.wireOp",EDGE,"E19.7")])]});
            var Q22;
            Q22=makeQuery(id+"F11.opExtrude","SWEPT_EDGE",EDGE,{"disambiguationData":[OSD([sQuery(id+"F10.wireOp",EDGE,"E19.5"),sQuery(id+"F10.wireOp",EDGE,"E19.6")])]});
            var Q23;
            {var subQ0=sQuery(id+"F7.wireOp",EDGE,"E15.right");var subQ1=sQuery(id+"F7.wireOp",EDGE,"E14.right");var subQ2=sQuery(id+"F7.wireOp",EDGE,"E13.left");var subQ3=sQuery(id+"F0.wireOp",EDGE,"E0.right");var subQ4=sQuery(id+"F0.wireOp",EDGE,"E0.left");var subQ5=sQuery(id+"F0.wireOp",EDGE,"E0.top");var subQ6=sQuery(id+"F0.wireOp",EDGE,"E0.bottom");var subQ7=sQuery(id+"F10.wireOp",EDGE,"E19.4");Q23=makeQuery(id+"F11.boolean.opBoolean","SPLIT",EDGE,{"disambiguationData":[TD([makeQuery(id+"F2.opShell","OFFSET_FACE",FACE,{"disambiguationData":[OSD([subQ6,subQ5,subQ4,subQ3])]})])],"derivedFrom":makeQuery(id+"F11.opExtrude","SWEPT_EDGE",EDGE,{"disambiguationData":[OSD([subQ2,subQ1,subQ0,subQ7])]})});}
            fillet(context, id + "F18", {"entities" : qUnion([Q0, Q1, Q2, Q3, Q4, Q5, Q6, Q7, Q8, Q9, Q10, Q11, Q12, Q13, Q14, Q15, Q16, Q17, Q18, Q19, Q20, Q21, Q22, Q23]), "radius" : 1 * mm, "tangentPropagation" : true, "allowEdgeOverflow" : false});
        }
        {
            var Q0;
            Q0=makeQuery(id+"F1.opExtrude","CAP_FACE",FACE,{"disambiguationData":[OSD([sQuery(id+"F0.wireOp",EDGE,"E0.bottom"),sQuery(id+"F0.wireOp",EDGE,"E0.top"),sQuery(id+"F0.wireOp",EDGE,"E0.left"),sQuery(id+"F0.wireOp",EDGE,"E0.right")])],"isStart":true});
            var sketch = newSketch(context, id + "F19", { "sketchPlane" : qUnion([Q0])});
            skText(sketch, "E25", { "text": "SYNAPTEC", "fontName": "Arimo-Bold.ttf"});
            const initialGuessF19  = {"E25": [-0.06723, -0.00882, 1, 0, 0.01764]};
            skSetInitialGuess(sketch, initialGuessF19);
            skSolve(sketch);
        }
        {
            var Q0;
            Q0=qSketchRegion(id+"F19",true);
            extrude(context, id + "F20", {"entities" : qUnion([Q0]), "operationType" : NewBodyOperationType.REMOVE, "oppositeDirection" : true, "depth" : 0.2 * mm});
        }
    });
